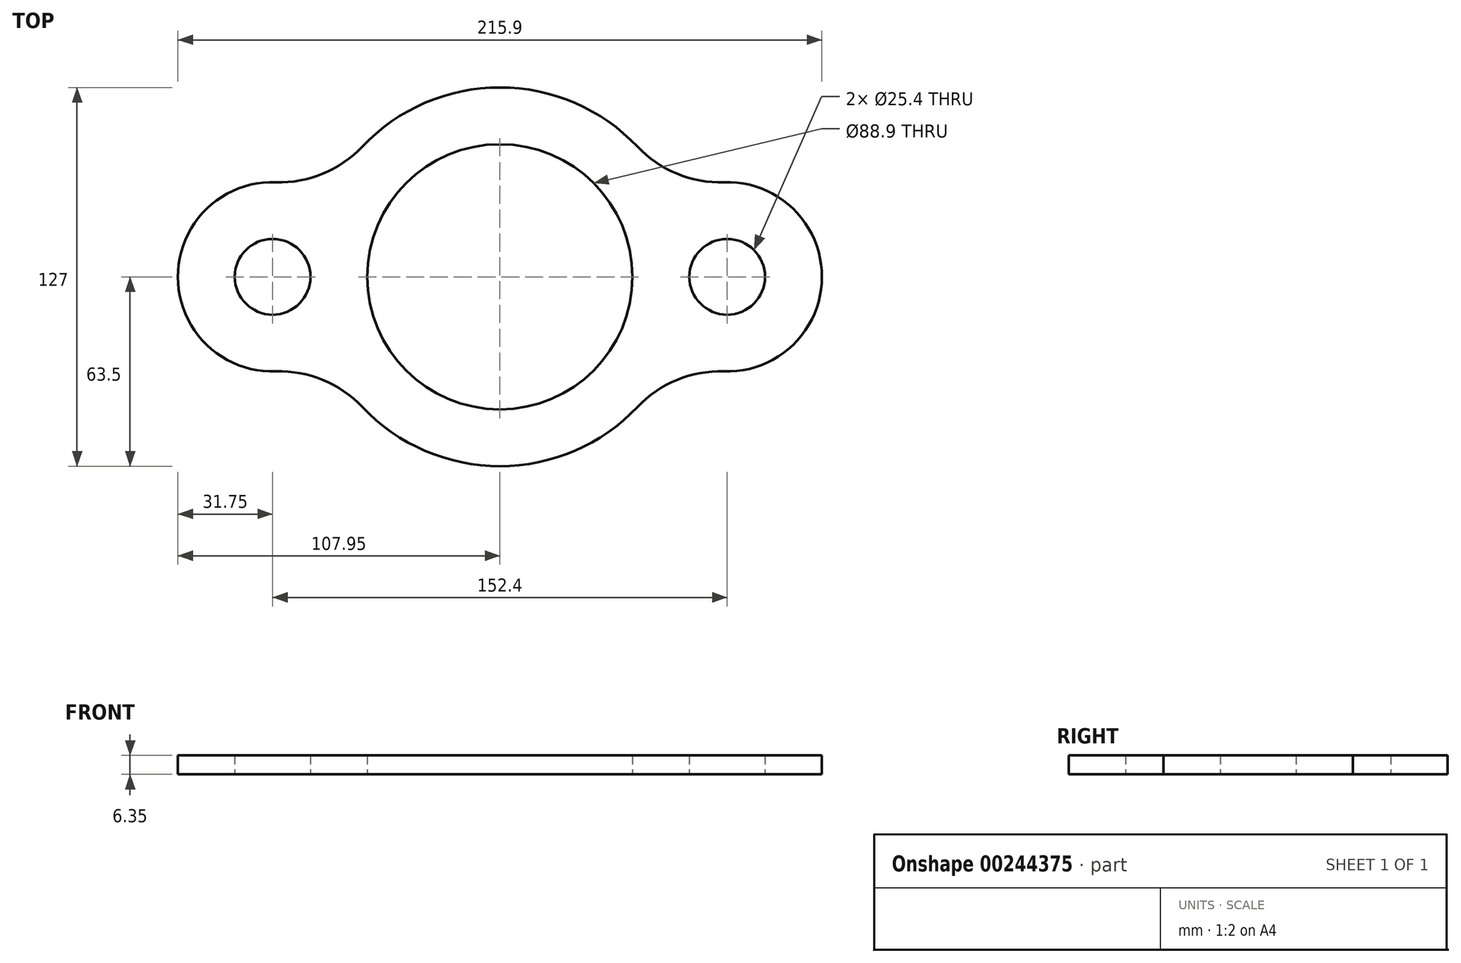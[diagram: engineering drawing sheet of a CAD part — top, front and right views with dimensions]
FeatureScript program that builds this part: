
annotation { "Feature Type Name" : "Feature", "Feature Type Description" : "" }
export const myFeature = defineFeature(function(context is Context, id is Id, definition is map)
    precondition{}
    {
        {
            var Q0;
            Q0=qCreatedBy(makeId("Top.planeOp"),FACE);
            var sketch = newSketch(context, id + "F0", { "sketchPlane" : qUnion([Q0])});
            skArc(sketch, "E0", {"start": v(-46.14, -43.63) * mm, "mid": v(0, -63.5) * mm, "end": v(46.14, -43.63) * mm});
            skCircle(sketch, "E1", {"center": v(0, 0) * mm, "radius": 44.45 * mm});
            skArc(sketch, "E2", {"start": v(75.12, -31.73) * mm, "mid": v(107.95, 0) * mm, "end": v(75.12, 31.73) * mm});
            skCircle(sketch, "E3", {"center": v(76.2, 0) * mm, "radius": 12.7 * mm});
            skArc(sketch, "E4", {"start": v(-75.12, 31.73) * mm, "mid": v(-107.95, 0) * mm, "end": v(-75.12, -31.73) * mm});
            skCircle(sketch, "E5", {"center": v(-76.2, 0) * mm, "radius": 12.7 * mm});
            skLineSegment(sketch, "E6", {"start": v(-76.2, 0) * mm, "end": v(0, 0) * mm, "construction": true});
            skLineSegment(sketch, "E7", {"start": v(0, 0) * mm, "end": v(76.2, 0) * mm, "construction": true});
            skArc(sketch, "E8.trimOffspring", {"start": v(46.14, 43.63) * mm, "mid": v(0, 63.5) * mm, "end": v(-46.14, 43.63) * mm});
            skPoint(sketch, "E9.visualSharp", {"position": v(-57.94, 25.98) * mm});
            skArc(sketch, "E9.filletArc", {"start": v(-75.12, 31.73) * mm, "mid": v(-59.35, 34.56) * mm, "end": v(-46.14, 43.63) * mm});
            skPoint(sketch, "E10.visualSharp", {"position": v(57.94, 25.98) * mm});
            skArc(sketch, "E10.filletArc", {"start": v(46.14, 43.63) * mm, "mid": v(59.35, 34.56) * mm, "end": v(75.12, 31.73) * mm});
            skPoint(sketch, "E11.visualSharp", {"position": v(57.94, -25.98) * mm});
            skArc(sketch, "E11.filletArc", {"start": v(75.12, -31.73) * mm, "mid": v(59.35, -34.56) * mm, "end": v(46.14, -43.63) * mm});
            skPoint(sketch, "E12.visualSharp", {"position": v(-57.94, -25.98) * mm});
            skArc(sketch, "E12.filletArc", {"start": v(-46.14, -43.63) * mm, "mid": v(-59.35, -34.56) * mm, "end": v(-75.12, -31.73) * mm});
            skSolve(sketch);
        }
        {
            var Q0;
            Q0=makeQuery(id+"F0.imprint","IMPRINT",FACE,{"disambiguationData":[TD([[makeQuery(id+"F0.imprint","IMPRINT",EDGE,{"derivedFrom":sQuery(id+"F0.wireOp",EDGE,"E0")}),1.0]])]});
            extrude(context, id + "F1", {"entities" : qUnion([Q0]), "depth" : 6.35 * mm});
        }
    });
